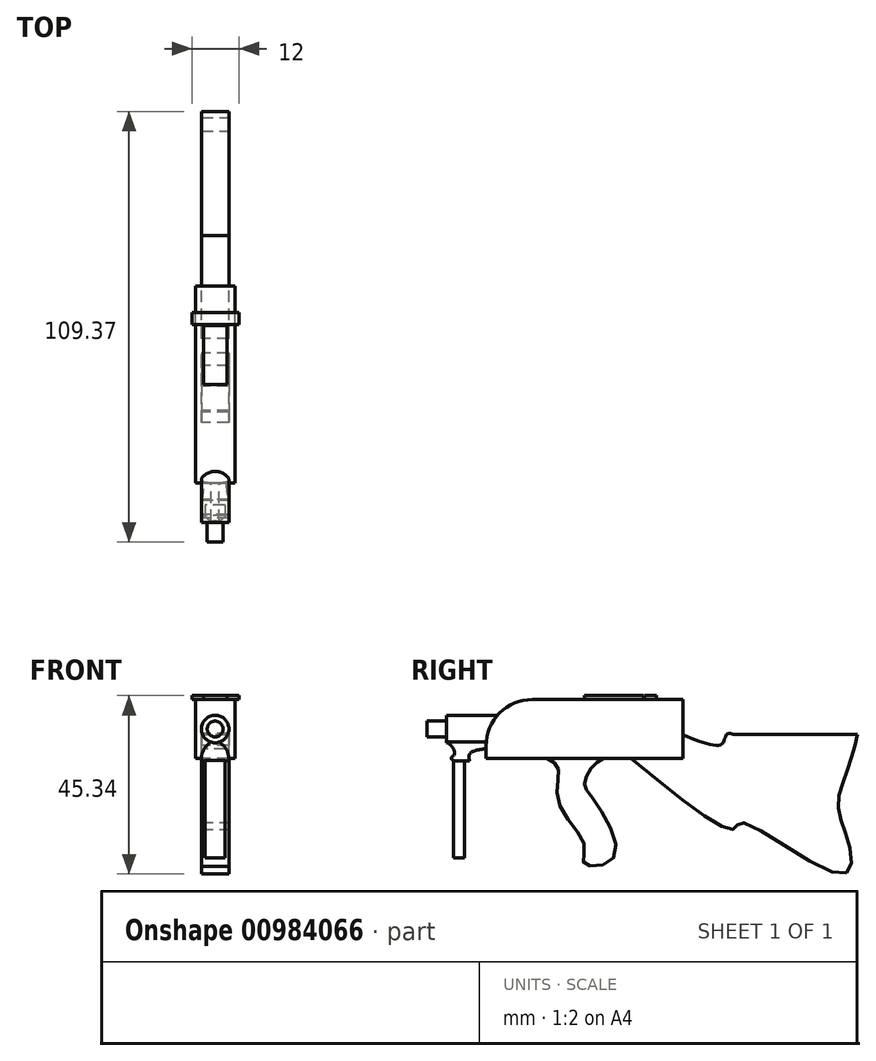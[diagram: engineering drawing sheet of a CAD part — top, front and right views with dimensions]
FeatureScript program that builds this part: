
annotation { "Feature Type Name" : "Feature", "Feature Type Description" : "" }
export const myFeature = defineFeature(function(context is Context, id is Id, definition is map)
    precondition{}
    {
        {
            var Q0;
            Q0=qCreatedBy(makeId("Right.planeOp"),FACE);
            var sketch = newSketch(context, id + "F0", { "sketchPlane" : qUnion([Q0])});
            skLineSegment(sketch, "E0.bottom", {"start": v(-25, -7.5) * mm, "end": v(25, -7.5) * mm});
            skLineSegment(sketch, "E0.top", {"start": v(-25, 7.5) * mm, "end": v(25, 7.5) * mm});
            skLineSegment(sketch, "E0.left", {"start": v(-25, -7.5) * mm, "end": v(-25, 7.5) * mm});
            skLineSegment(sketch, "E0.right", {"start": v(25, -7.5) * mm, "end": v(25, 7.5) * mm});
            skPoint(sketch, "E0.middle", {"position": v(0, 0) * mm});
            skSolve(sketch);
        }
        {
            var Q0;
            Q0=qCreatedBy(makeId("Right.planeOp"),FACE);
            var sketch = newSketch(context, id + "F1", { "sketchPlane" : qUnion([Q0])});
            skFitSpline(sketch, "E1", {"points": [v(5.03, -7.4) * mm, v(1.78, -9.8) * mm, v(0, -13.91) * mm, v(1.78, -17.16) * mm, v(7.6, -32.4) * mm, v(0, -34.28) * mm, v(0, -29.83) * mm, v(-6.6, -18.36) * mm, v(-6.78, -9.8) * mm, v(-10.2, -7.24) * mm], "startDerivative": vector(-40.7, -22.24) * mm, "endDerivative": vector(-50.92, 21) * mm});
            skLineSegment(sketch, "E2", {"start": v(-10.2, -7.24) * mm, "end": v(5.03, -7.4) * mm});
            skSolve(sketch);
        }
        {
            var Q0;
            Q0=qCreatedBy(makeId("Right.planeOp"),FACE);
            var sketch = newSketch(context, id + "F2", { "sketchPlane" : qUnion([Q0])});
            skFitSpline(sketch, "E3", {"points": [v(-10.77, -7.47) * mm, v(-10.46, -11.48) * mm, v(-13.07, -13.88) * mm, v(-11.27, -11.38) * mm, v(-12.17, -7.47) * mm, v(-10.77, -7.47) * mm]});
            skSolve(sketch);
        }
        {
            var Q0;
            Q0=qCreatedBy(makeId("Right.planeOp"),FACE);
            var sketch = newSketch(context, id + "F3", { "sketchPlane" : qUnion([Q0])});
            skFitSpline(sketch, "E4", {"points": [v(11.48, -7.28) * mm, v(38.12, -25.4) * mm, v(39.73, -23.7) * mm, v(65.77, -36.83) * mm, v(66.97, -28.51) * mm, v(64.47, -18.9) * mm, v(67.17, -9.39) * mm, v(69.37, -1.37) * mm], "startDerivative": vector(158.2, -127.96) * mm, "endDerivative": vector(15.45, 66.53) * mm});
            skLineSegment(sketch, "E5", {"start": v(69.37, -1.37) * mm, "end": v(37.82, -1.37) * mm});
            skFitSpline(sketch, "E6", {"points": [v(37.82, -1.37) * mm, v(36.12, -1.37) * mm, v(34.92, -3.78) * mm, v(24.7, -1.37) * mm], "startDerivative": vector(-9.48, 2.64) * mm, "endDerivative": vector(-25.05, 10.22) * mm});
            skLineSegment(sketch, "E7", {"start": v(24.7, -1.37) * mm, "end": v(24.7, -7.28) * mm});
            skLineSegment(sketch, "E8", {"start": v(24.7, -7.28) * mm, "end": v(11.48, -7.28) * mm});
            skSolve(sketch);
        }
        {
            var Q0;
            Q0=makeQuery(id+"F0.imprint","IMPRINT",FACE,{"disambiguationData":[TD([[makeQuery(id+"F0.imprint","IMPRINT",EDGE,{"derivedFrom":sQuery(id+"F0.wireOp",EDGE,"E0.bottom")}),1.0]])]});
            extrude(context, id + "F4", {"entities" : qUnion([Q0]), "endBound" : BoundingType.SYMMETRIC, "depth" : 10 * mm, "offsetDistance" : 25 * mm});
        }
        {
            var Q0;
            Q0=sQuery(id+"F2.wireOp",EDGE,"E3");
            extrude(context, id + "F5", {"bodyType" : ToolBodyType.SURFACE, "surfaceEntities" : qUnion([Q0]), "endBound" : BoundingType.SYMMETRIC, "depth" : 5 * mm, "offsetDistance" : 25 * mm});
        }
        {
            var Q0;
            Q0=makeQuery(id+"F1.imprint","IMPRINT",FACE,{"disambiguationData":[TD([[makeQuery(id+"F1.imprint","IMPRINT",EDGE,{"derivedFrom":sQuery(id+"F1.wireOp",EDGE,"E1")}),-1.0]])]});
            extrude(context, id + "F6", {"entities" : qUnion([Q0]), "operationType" : NewBodyOperationType.ADD, "endBound" : BoundingType.SYMMETRIC, "depth" : 7 * mm, "offsetDistance" : 25 * mm});
        }
        {
            var Q0;
            Q0=makeQuery(id+"F3.imprint","IMPRINT",FACE,{"disambiguationData":[TD([[makeQuery(id+"F3.imprint","IMPRINT",EDGE,{"derivedFrom":sQuery(id+"F3.wireOp",EDGE,"E4")}),1.0]])]});
            extrude(context, id + "F7", {"entities" : qUnion([Q0]), "operationType" : NewBodyOperationType.ADD, "endBound" : BoundingType.SYMMETRIC, "depth" : 7 * mm, "offsetDistance" : 25 * mm});
        }
        {
            var Q0;
            Q0=makeQuery(id+"F4.opExtrude","SWEPT_FACE",FACE,{"disambiguationData":[OSD([sQuery(id+"F0.wireOp",EDGE,"E0.left")])]});
            var sketch = newSketch(context, id + "F8", { "sketchPlane" : qUnion([Q0])});
            skCircle(sketch, "E9", {"center": v(0, 0) * mm, "radius": 3.5 * mm});
            skSolve(sketch);
        }
        {
            var Q0;
            Q0=makeQuery(id+"F8.imprint","IMPRINT",FACE,{"disambiguationData":[TD([[makeQuery(id+"F8.imprint","IMPRINT",EDGE,{"derivedFrom":sQuery(id+"F8.wireOp",EDGE,"E9")}),1.0]])]});
            extrude(context, id + "F9", {"entities" : qUnion([Q0]), "operationType" : NewBodyOperationType.ADD, "endBound" : BoundingType.SYMMETRIC, "depth" : 20 * mm, "offsetDistance" : 25 * mm});
        }
        {
            var Q0;
            Q0=qCreatedBy(makeId("Right.planeOp"),FACE);
            var sketch = newSketch(context, id + "F10", { "sketchPlane" : qUnion([Q0])});
            skFitSpline(sketch, "E10", {"points": [v(-25, -5.01) * mm, v(-27.75, -5.49) * mm, v(-29.12, -6.32) * mm, v(-29.17, -8.05) * mm], "startDerivative": vector(-7.3, -0.94) * mm, "endDerivative": vector(2.8, -6.17) * mm});
            skLineSegment(sketch, "E11", {"start": v(-29.17, -8.05) * mm, "end": v(-33.17, -8.05) * mm});
            skFitSpline(sketch, "E12", {"points": [v(-33.17, -8.05) * mm, v(-33.88, -7.45) * mm, v(-33.17, -6.62) * mm, v(-33.17, -5.3) * mm, v(-33.94, -4.18) * mm, v(-34.71, -3.34) * mm], "startDerivative": vector(-6.15, 3.22) * mm, "endDerivative": vector(-3.87, 4.06) * mm});
            skLineSegment(sketch, "E13", {"start": v(-34.71, -3.34) * mm, "end": v(-25.07, -3.34) * mm});
            skLineSegment(sketch, "E14", {"start": v(-25.07, -3.34) * mm, "end": v(-25, -5.01) * mm});
            skSolve(sketch);
        }
        {
            var Q0;
            Q0=makeQuery(id+"F10.imprint","IMPRINT",FACE,{"disambiguationData":[TD([[makeQuery(id+"F10.imprint","IMPRINT",EDGE,{"derivedFrom":sQuery(id+"F10.wireOp",EDGE,"E10")}),-1.0]])]});
            extrude(context, id + "F11", {"entities" : qUnion([Q0]), "operationType" : NewBodyOperationType.ADD, "endBound" : BoundingType.SYMMETRIC, "depth" : 7 * mm, "offsetDistance" : 25 * mm});
        }
        {
            var Q0;
            Q0=makeQuery(id+"F11.opExtrude","CAP_EDGE",EDGE,{"disambiguationData":[OSD([sQuery(id+"F10.wireOp",EDGE,"E13")])],"isStart":false});
            var Q1;
            Q1=makeQuery(id+"F11.opExtrude","CAP_EDGE",EDGE,{"disambiguationData":[OSD([sQuery(id+"F10.wireOp",EDGE,"E13")])],"isStart":true});
            fillet(context, id + "F12", {"entities" : qUnion([Q0, Q1]), "radius" : 5 * mm, "tangentPropagation" : true, "allowEdgeOverflow" : false});
        }
        {
            var Q0;
            Q0=qCreatedBy(makeId("Right.planeOp"),FACE);
            var sketch = newSketch(context, id + "F13", { "sketchPlane" : qUnion([Q0])});
            skLineSegment(sketch, "E15.bottom", {"start": v(-30.53, -32.73) * mm, "end": v(-33.22, -32.73) * mm});
            skLineSegment(sketch, "E15.top", {"start": v(-30.53, -7.1) * mm, "end": v(-33.22, -7.1) * mm});
            skLineSegment(sketch, "E15.left", {"start": v(-30.53, -32.73) * mm, "end": v(-30.53, -7.1) * mm});
            skLineSegment(sketch, "E15.right", {"start": v(-33.22, -32.73) * mm, "end": v(-33.22, -7.1) * mm});
            skPoint(sketch, "E15.middle", {"position": v(-31.88, -19.91) * mm});
            skSolve(sketch);
        }
        {
            var Q0;
            Q0=makeQuery(id+"F13.imprint","IMPRINT",FACE,{"disambiguationData":[TD([[makeQuery(id+"F13.imprint","IMPRINT",EDGE,{"derivedFrom":sQuery(id+"F13.wireOp",EDGE,"E15.bottom")}),-1.0]])]});
            extrude(context, id + "F14", {"entities" : qUnion([Q0]), "operationType" : NewBodyOperationType.ADD, "endBound" : BoundingType.SYMMETRIC, "depth" : 5 * mm, "offsetDistance" : 25 * mm});
        }
        {
            var Q0;
            Q0=makeQuery(id+"F4.opExtrude","SWEPT_FACE",FACE,{"disambiguationData":[OSD([sQuery(id+"F0.wireOp",EDGE,"E0.top")])]});
            var sketch = newSketch(context, id + "F15", { "sketchPlane" : qUnion([Q0])});
            skLineSegment(sketch, "E16.bottom", {"start": v(-2.98, 0) * mm, "end": v(3.02, 0) * mm});
            skLineSegment(sketch, "E16.top", {"start": v(-2.98, 15) * mm, "end": v(3.02, 15) * mm});
            skLineSegment(sketch, "E16.left", {"start": v(-2.98, 0) * mm, "end": v(-2.98, 15) * mm});
            skLineSegment(sketch, "E16.right", {"start": v(3.02, 0) * mm, "end": v(3.02, 15) * mm});
            skSolve(sketch);
        }
        {
            var Q0;
            Q0=makeQuery(id+"F15.imprint","IMPRINT",FACE,{"disambiguationData":[TD([[makeQuery(id+"F15.imprint","IMPRINT",EDGE,{"derivedFrom":sQuery(id+"F15.wireOp",EDGE,"E16.bottom")}),-1.0]])]});
            var sketch = newSketch(context, id + "F16", { "sketchPlane" : qUnion([Q0])});
            skLineSegment(sketch, "E17.bottom", {"start": v(-5.89, 15.26) * mm, "end": v(6.11, 15.26) * mm});
            skLineSegment(sketch, "E17.top", {"start": v(-5.89, 18.26) * mm, "end": v(6.11, 18.26) * mm});
            skLineSegment(sketch, "E17.left", {"start": v(-5.89, 15.26) * mm, "end": v(-5.89, 18.26) * mm});
            skLineSegment(sketch, "E17.right", {"start": v(6.11, 15.26) * mm, "end": v(6.11, 18.26) * mm});
            skSolve(sketch);
        }
        {
            var Q0;
            {var subQ0=sQuery(id+"F16.wireOp",EDGE,"E17.bottom");var subQ1=sQuery(id+"F0.wireOp",EDGE,"E0.top");var subQ2=makeQuery(id+"F15.imprint","IMPRINT",EDGE,{"derivedFrom":makeQuery(id+"F4.opExtrude","CAP_EDGE",EDGE,{"disambiguationData":[OSD([subQ1])],"isStart":true})});var subQ3=makeQuery(id+"F16.imprint","INTERSECT",VERTEX,{"derivedFrom":[subQ2,subQ0]});Q0=makeQuery(id+"F16.imprint","IMPRINT",FACE,{"disambiguationData":[TD([[makeQuery(id+"F16.imprint","IMPRINT",EDGE,{"disambiguationData":[TD([[subQ3,-1.0]])],"derivedFrom":subQ0}),1.0]])]});}
            var Q1;
            {var subQ0=sQuery(id+"F16.wireOp",EDGE,"E17.left");Q1=makeQuery(id+"F16.imprint","IMPRINT",FACE,{"disambiguationData":[TD([[makeQuery(id+"F16.imprint","IMPRINT",EDGE,{"derivedFrom":subQ0}),-1.0]])]});}
            var Q2;
            {var subQ0=sQuery(id+"F16.wireOp",EDGE,"E17.right");Q2=makeQuery(id+"F16.imprint","IMPRINT",FACE,{"disambiguationData":[TD([[makeQuery(id+"F16.imprint","IMPRINT",EDGE,{"derivedFrom":subQ0}),1.0]])]});}
            extrude(context, id + "F17", {"entities" : qUnion([Q0, Q1, Q2]), "operationType" : NewBodyOperationType.ADD, "depth" : 1 * mm, "offsetDistance" : 25 * mm});
        }
        {
            var Q0;
            Q0=makeQuery(id+"F15.imprint","IMPRINT",FACE,{"disambiguationData":[TD([[makeQuery(id+"F15.imprint","IMPRINT",EDGE,{"derivedFrom":sQuery(id+"F15.wireOp",EDGE,"E16.bottom")}),1.0]])]});
            extrude(context, id + "F18", {"entities" : qUnion([Q0]), "operationType" : NewBodyOperationType.ADD, "depth" : 1 * mm, "offsetDistance" : 25 * mm});
        }
        {
            var Q0;
            Q0=makeQuery(id+"F9.opExtrude","CAP_FACE",FACE,{"disambiguationData":[OSD([sQuery(id+"F8.wireOp",EDGE,"E9")])],"isStart":false});
            var sketch = newSketch(context, id + "F19", { "sketchPlane" : qUnion([Q0])});
            skCircle(sketch, "E18", {"center": v(0, 0) * mm, "radius": 2 * mm});
            skSolve(sketch);
        }
        {
            var Q0;
            Q0=makeQuery(id+"F19.imprint","IMPRINT",FACE,{"disambiguationData":[TD([[makeQuery(id+"F19.imprint","IMPRINT",EDGE,{"derivedFrom":sQuery(id+"F19.wireOp",EDGE,"E18")}),1.0]])]});
            extrude(context, id + "F20", {"entities" : qUnion([Q0]), "operationType" : NewBodyOperationType.ADD, "depth" : 5 * mm, "offsetDistance" : 25 * mm});
        }
        {
            var Q0;
            Q0=makeQuery(id+"F20.opExtrude","CAP_FACE",FACE,{"disambiguationData":[OSD([sQuery(id+"F19.wireOp",EDGE,"E18")])],"isStart":false});
            var sketch = newSketch(context, id + "F21", { "sketchPlane" : qUnion([Q0])});
            skCircle(sketch, "E19", {"center": v(0, 0) * mm, "radius": 1 * mm});
            skSolve(sketch);
        }
        {
            var Q0;
            Q0=sQuery(id+"F21.wireOp",EDGE,"E19");
            extrude(context, id + "F22", {"bodyType" : ToolBodyType.SURFACE, "surfaceEntities" : qUnion([Q0]), "depth" : 35 * mm, "offsetDistance" : 25 * mm});
        }
        {
            var Q0;
            Q0=makeQuery(id+"F4.opExtrude","SWEPT_EDGE",EDGE,{"disambiguationData":[OSD([sQuery(id+"F0.wireOp",EDGE,"E0.top"),sQuery(id+"F0.wireOp",EDGE,"E0.left")])]});
            fillet(context, id + "F23", {"entities" : qUnion([Q0]), "radius" : 11.83 * mm, "tangentPropagation" : true, "allowEdgeOverflow" : false});
        }
    });
